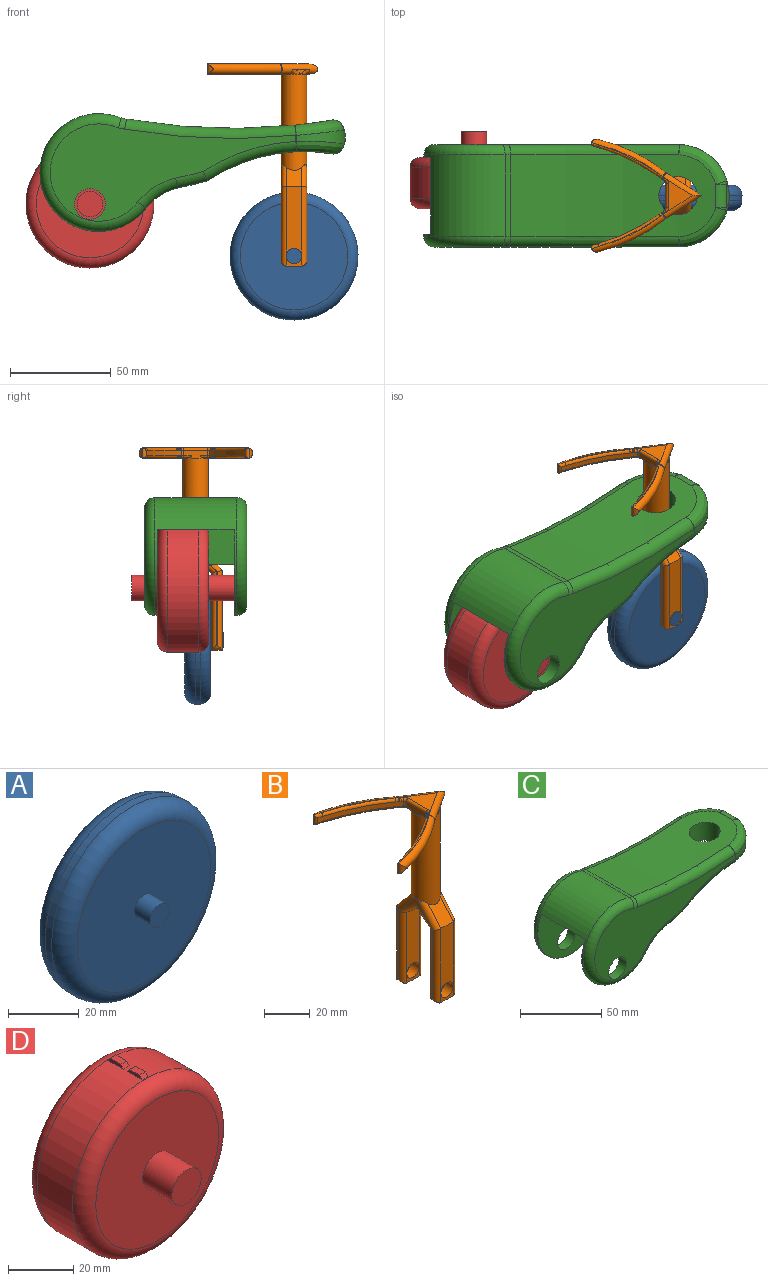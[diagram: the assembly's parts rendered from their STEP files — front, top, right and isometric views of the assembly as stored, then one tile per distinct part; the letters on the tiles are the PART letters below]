
ASSEMBLY  parts=4 mates=3
PART A: 9 faces, bbox 68.7x25.4x68.7 mm
  f0: cylinder r=31.75mm len=63.5mm, axis (0,1,0), area 506.7mm2, adj f7,f8
  f1: plane 53.34x53.34mm, normal (0,-1,0), area 2189mm2, adj f5,f8
  f2: plane 53.34x53.34mm, normal (0,1,0), area 2189mm2, adj f4,f7
  f3: plane 7.62x7.62mm, normal (0,1,0), area 45.6mm2, adj f4
  f4: cylinder r=3.81mm len=7.62mm, axis (0,1,0), area 152mm2, adj f2,f3
  f5: cylinder r=3.81mm len=7.62mm, axis (0,1,0), area 152mm2, adj f1,f6
  f6: plane 7.62x7.62mm, normal (0,-1,0), area 45.6mm2, adj f5
  f7: torus R=26.67mm, axis (0,-1,0), area 1499.3mm2, adj f0,f2
  f8: torus R=26.67mm, axis (0,-1,0), area 1499.3mm2, adj f0,f1
PART B: 110 faces, bbox 59x71.6x101.6 mm
  f0: plane 7.62x4.94mm, normal (0,1,0), area 14.9mm2, adj f19,f88,f99,f109
  f1: plane 7.62x4.94mm, normal (0,-1,0), area 14.9mm2, adj f19,f85,f97,f109
  f2: plane 33.04x7.62mm, normal (0,-1,0), area 229mm2, adj f29,f92,f104,f108
  f3: plane 34.65x7.62mm, normal (0,1,0), area 241.2mm2, adj f30,f93,f103,f108
  f4: plane 36.27x0.13mm, normal (1,0,0), area 4.6mm2, adj f101,f103,f104,f107
  f5: plane 18.75x10.49mm, normal (1,0,0), area 31mm2, adj f98,f100,f102,f105,f106,f107
  f6: plane 36.27x0.13mm, normal (-1,0,0), area 4.6mm2, adj f90,f92,f93,f95
  f7: plane 36.27x0.13mm, normal (-1,0,0), area 4.6mm2, adj f85,f86,f87,f88
  f8: plane 30.79x14.98mm, normal (0,0,1), area 8.5mm2, adj f42,f60
  f9: plane 17.61x13.75mm, normal (0,0,1), area 89.8mm2, adj f43,f47,f70,f74,f76,f77,f79
  f10: plane 30.79x14.98mm, normal (0,0,-1), area 8.5mm2, adj f37,f51
  f11: plane 4.55x4.46mm, normal (0,0,-1), area 4.2mm2, adj f13,f47,f80,f82,f83
  f12: plane 12.1x3.81mm, normal (-1,0,0), area 36.1mm2, adj f13,f14,f63,f71,f77,f81,f83
  f13: cylinder r=6.35mm len=48.93mm, axis (0,0,-1), area 1836.4mm2, adj f11,f12,f14,f17,f23,f27,f30,f39
  f14: plane 4.23x0.36mm, normal (0,0,1), area 1mm2, adj f12,f13
  f15: plane 33.04x7.62mm, normal (0,1,0), area 229mm2, adj f16,f88,f99,f109
  f16: plane 7.88x7.62mm, normal (0,0.63,-0.78), area 77.4mm2, adj f15,f29,f89,f102
  f17: plane 9.44x8.01mm, normal (0,-0.76,0.65), area 84.1mm2, adj f13,f18,f87,f100
  f18: plane 34.65x7.62mm, normal (0,-1,0), area 241.2mm2, adj f17,f85,f97,f109
  f19: plane 7.62x5.21mm, normal (0,0,-1), area 39.7mm2, adj f0,f1,f86,f96
  f20: plane 36.27x0.13mm, normal (1,0,0), area 4.6mm2, adj f96,f97,f99,f100
  f21: plane 18.75x10.49mm, normal (-1,0,0), area 31mm2, adj f84,f87,f89,f91,f94,f95
  f22: plane 30.79x14.98mm, normal (0,0,-1), area 8.5mm2, adj f42,f68
  f23: plane 0.94x0.74mm, normal (0,0,-1), area 0.3mm2, adj f13,f43,f47
  f24: plane 9.55x6.47mm, normal (0.54,0.84,0), area 9.2mm2, adj f45,f47,f48
  f25: plane 30.79x14.98mm, normal (0,0,1), area 8.5mm2, adj f37,f54
  f26: plane 9.55x6.47mm, normal (0.54,-0.84,0), area 9.2mm2, adj f39,f43,f46
  f27: plane 4.55x4.46mm, normal (0,0,-1), area 4.2mm2, adj f13,f43,f62,f63,f67
  f28: plane 7.62x4.94mm, normal (0,-1,0), area 14.9mm2, adj f32,f92,f104,f108
  f29: plane 7.88x7.62mm, normal (0,-0.63,-0.78), area 77.4mm2, adj f2,f16,f91,f105
  f30: plane 9.44x8.01mm, normal (0,0.76,0.65), area 84.1mm2, adj f3,f13,f95,f107
  f31: plane 7.62x4.94mm, normal (0,1,0), area 14.9mm2, adj f32,f93,f103,f108
  f32: plane 7.62x5.21mm, normal (0,0,-1), area 39.7mm2, adj f28,f31,f90,f101
  f33: plane 4.98x0.24mm, normal (-0.87,-0.5,0), area 1.4mm2, adj f37,f38,f50
  f34: cylinder r=101.49mm len=35.64mm, axis (0,0,1), area 101.6mm2, adj f49,f50,f51,f52,f53,f54,f55,f57
  f35: plane 4.98x0.24mm, normal (-0.87,0.5,0), area 1.4mm2, adj f41,f42,f59
  f36: cylinder r=101.49mm len=35.64mm, axis (0,0,1), area 101.6mm2, adj f56,f59,f60,f64,f65,f68,f69,f72
  f37: torus R=82.07mm, axis (0,0,1), area 311.6mm2, adj f10,f25,f33,f38,f40,f49,f50,f52
  f38: cylinder r=2.54mm len=4.84mm, axis (0,0,1), area 7.8mm2, adj f33,f37
  f39: bspline ~5.77x2.86mm, area 6.4mm2, adj f13,f26,f43
  f40: torus R=5.08mm, axis (0,0,1), area 2.9mm2, adj f37,f43,f55,f61
  f41: cylinder r=2.54mm len=4.84mm, axis (0,0,1), area 7.8mm2, adj f35,f42
  f42: torus R=82.07mm, axis (0,0,1), area 311.6mm2, adj f8,f22,f35,f41,f44,f56,f59,f64
  f43: cylinder r=2.54mm len=19.03mm, axis (-0.84,-0.54,0), area 115.1mm2, adj f9,f23,f26,f27,f39,f40,f46,f47
  f44: torus R=5.08mm, axis (0,0,1), area 2.9mm2, adj f42,f47,f69,f75
  f45: bspline ~5.77x2.86mm, area 6.4mm2, adj f13,f24,f47
  f46: bspline ~5.01x4.47mm, area 6.2mm2, adj f13,f26,f43
  f47: cylinder r=2.54mm len=19.03mm, axis (-0.84,0.54,0), area 115.1mm2, adj f9,f11,f23,f24,f43,f44,f45,f48
  f48: bspline ~5.01x4.47mm, area 6.2mm2, adj f13,f24,f47
  f49: bspline ~8.42x3.73mm, area 6.4mm2, adj f34,f37,f50,f51
  f50: cylinder r=1.27mm len=5.06mm, axis (0,0,1), area 9.9mm2, adj f33,f34,f37,f49,f52
  f51: torus R=102.76mm, axis (0,0,1), area 68.1mm2, adj f10,f34,f49,f53
  f52: bspline ~8.42x3.73mm, area 6.4mm2, adj f34,f37,f50,f54
  f53: bspline ~4.52x3.64mm, area 2.4mm2, adj f34,f37,f51,f55
  f54: torus R=102.76mm, axis (0,0,1), area 68.1mm2, adj f25,f34,f52,f57
  f55: bspline ~1.92x1.9mm, area 1.1mm2, adj f34,f40,f53,f58
  f56: bspline ~8.42x3.73mm, area 6.4mm2, adj f36,f42,f59,f60
  f57: bspline ~4.52x3.64mm, area 2.4mm2, adj f34,f37,f54,f61
  f58: bspline ~3.89x3.56mm, area 1.3mm2, adj f34,f43,f55,f62
  f59: cylinder r=1.27mm len=5.06mm, axis (0,0,1), area 9.9mm2, adj f35,f36,f42,f56,f64
  f60: torus R=102.76mm, axis (0,0,1), area 68.1mm2, adj f8,f36,f56,f65
  f61: bspline ~1.98x1.98mm, area 1.1mm2, adj f34,f40,f57,f66
  f62: torus R=102.76mm, axis (0,0,1), area 2.4mm2, adj f27,f34,f58,f67
  f63: cylinder r=1.27mm len=3.93mm, axis (0,1,0), area 5.7mm2, adj f12,f13,f27,f67
  f64: bspline ~8.42x3.73mm, area 6.4mm2, adj f36,f42,f59,f68
  f65: bspline ~4.52x3.64mm, area 2.4mm2, adj f36,f42,f60,f69
  f66: bspline ~3.89x3.56mm, area 1.3mm2, adj f34,f43,f61,f70
  f67: torus R=2.54mm, axis (0,0,1), area 3.2mm2, adj f27,f62,f63,f71
  f68: torus R=102.76mm, axis (0,0,1), area 68.1mm2, adj f22,f36,f64,f72
  f69: bspline ~1.92x1.9mm, area 1.1mm2, adj f36,f44,f65,f73
  f70: torus R=102.76mm, axis (0,0,1), area 2.4mm2, adj f9,f34,f66,f74
  f71: cylinder r=1.27mm len=2.54mm, axis (0,0,1), area 3mm2, adj f12,f34,f67,f74
  f72: bspline ~4.52x3.64mm, area 2.4mm2, adj f36,f42,f68,f75
  f73: bspline ~3.89x3.56mm, area 1.3mm2, adj f36,f47,f69,f76
  f74: torus R=2.54mm, axis (0,0,1), area 3.2mm2, adj f9,f70,f71,f77
  f75: bspline ~1.98x1.98mm, area 1.1mm2, adj f36,f44,f72,f78
  f76: torus R=102.76mm, axis (0,0,1), area 2.4mm2, adj f9,f36,f73,f79
  f77: cylinder r=1.27mm len=12.1mm, axis (0,1,0), area 24.1mm2, adj f9,f12,f74,f79
  f78: bspline ~3.89x3.56mm, area 1.3mm2, adj f36,f47,f75,f80
  f79: torus R=2.54mm, axis (0,0,1), area 3.2mm2, adj f9,f76,f77,f81
  f80: torus R=102.76mm, axis (0,0,1), area 2.4mm2, adj f11,f36,f78,f82
  f81: cylinder r=1.27mm len=2.54mm, axis (0,0,1), area 3mm2, adj f12,f36,f79,f82
  f82: torus R=2.54mm, axis (0,0,1), area 3.2mm2, adj f11,f80,f81,f83
  f83: cylinder r=1.27mm len=3.93mm, axis (0,-1,0), area 5.7mm2, adj f11,f12,f13,f82
  f84: bspline ~3.77x2.18mm, area 1.6mm2, adj f13,f21,f87
  f85: cylinder r=2.54mm len=39.59mm, axis (0,0,-1), area 151mm2, adj f1,f7,f18,f86,f87
  f86: cylinder r=2.54mm len=5.21mm, axis (0,1,0), area 13.4mm2, adj f7,f19,f85,f88
  f87: cylinder r=2.54mm len=12.75mm, axis (0,-0.65,-0.76), area 54.4mm2, adj f7,f13,f17,f21,f84,f85,f88,f89
  f88: cylinder r=2.54mm len=39.14mm, axis (0,0,1), area 149.6mm2, adj f0,f7,f15,f86,f87,f89
  f89: cylinder r=2.54mm len=11.98mm, axis (0,0.78,0.63), area 46.9mm2, adj f16,f21,f87,f88,f91
  f90: cylinder r=2.54mm len=5.21mm, axis (0,-1,0), area 13.4mm2, adj f6,f32,f92,f93
  f91: cylinder r=2.54mm len=11.98mm, axis (0,-0.78,0.63), area 46.9mm2, adj f21,f29,f89,f92,f95
  f92: cylinder r=2.54mm len=39.14mm, axis (0,0,1), area 149.6mm2, adj f2,f6,f28,f90,f91,f95
  f93: cylinder r=2.54mm len=39.59mm, axis (0,0,-1), area 151mm2, adj f3,f6,f31,f90,f95
  f94: bspline ~3.77x2.18mm, area 1.6mm2, adj f13,f21,f95
  f95: cylinder r=2.54mm len=12.75mm, axis (0,0.65,-0.76), area 54.4mm2, adj f6,f13,f21,f30,f91,f92,f93,f94
  f96: cylinder r=2.54mm len=5.21mm, axis (0,-1,0), area 13.4mm2, adj f19,f20,f97,f99
  f97: cylinder r=2.54mm len=39.59mm, axis (0,0,1), area 151mm2, adj f1,f18,f20,f96,f100
  f98: bspline ~3.77x2.18mm, area 1.6mm2, adj f5,f13,f100
  f99: cylinder r=2.54mm len=39.14mm, axis (0,0,-1), area 149.6mm2, adj f0,f15,f20,f96,f100,f102
  f100: cylinder r=2.54mm len=12.75mm, axis (0,0.65,0.76), area 54.4mm2, adj f5,f13,f17,f20,f97,f98,f99,f102
  f101: cylinder r=2.54mm len=5.21mm, axis (0,1,0), area 13.4mm2, adj f4,f32,f103,f104
  f102: cylinder r=2.54mm len=11.98mm, axis (0,-0.78,-0.63), area 46.9mm2, adj f5,f16,f99,f100,f105
  f103: cylinder r=2.54mm len=39.59mm, axis (0,0,1), area 151mm2, adj f3,f4,f31,f101,f107
  f104: cylinder r=2.54mm len=39.14mm, axis (0,0,-1), area 149.6mm2, adj f2,f4,f28,f101,f105,f107
  f105: cylinder r=2.54mm len=11.98mm, axis (0,0.78,-0.63), area 46.9mm2, adj f5,f29,f102,f104,f107
  f106: bspline ~3.77x2.18mm, area 1.6mm2, adj f5,f13,f107
  f107: cylinder r=2.54mm len=12.75mm, axis (0,-0.65,0.76), area 54.4mm2, adj f4,f5,f13,f30,f103,f104,f105,f106
  f108: cylinder r=3.81mm len=7.62mm, axis (0,1,0), area 124.6mm2, adj f2,f3,f28,f31
  f109: cylinder r=3.81mm len=7.62mm, axis (0,1,0), area 124.6mm2, adj f0,f1,f15,f18
PART C: 53 faces, bbox 153.9x50.9x63.3 mm
  f0: plane 38.1x28.36mm, normal (0,0,-1), area 1080.7mm2, adj f16,f17,f18,f50
  f1: cylinder r=28.25mm len=15.73mm, axis (0,1,0), area 24mm2, adj f2,f6,f17,f27
  f2: cylinder r=225.55mm len=14.86mm, axis (0,1,0), area 19.4mm2, adj f1,f3,f17,f29
  f3: cylinder r=85.3mm len=61.7mm, axis (0,1,0), area 2195mm2, adj f2,f8,f14,f18,f24,f31,f42,f44
  f4: cylinder r=13.12mm len=10.14mm, axis (0,1,0), area 26.3mm2, adj f44,f45
  f5: cylinder r=299.81mm len=101.73mm, axis (0,1,0), area 3719.3mm2, adj f10,f14,f23,f30,f34,f37,f39
  f6: cylinder r=29.25mm len=58.5mm, axis (0,1,0), area 1978.8mm2, adj f1,f7,f10,f15,f16,f17,f19,f26
  f7: cylinder r=28.25mm len=15.73mm, axis (0,1,0), area 24mm2, adj f6,f8,f16,f20
  f8: cylinder r=225.55mm len=14.86mm, axis (0,1,0), area 19.4mm2, adj f3,f7,f16,f22
  f9: cylinder r=13.12mm len=11.48mm, axis (0,1,0), area 34.1mm2, adj f36,f37
  f10: cylinder r=38.9mm len=40.64mm, axis (0,1,0), area 115mm2, adj f5,f6,f21,f28
  f11: plane 121.94x48.34mm, normal (0,-1,0), area 2650.8mm2, adj f19,f20,f21,f22,f23,f24,f25,f52
  f12: plane 121.94x48.34mm, normal (0,1,0), area 2650.8mm2, adj f26,f27,f28,f29,f30,f31,f32,f51
  f13: cylinder r=25.42mm len=50.79mm, axis (0,0,-1), area 355.2mm2, adj f25,f32,f34,f36,f39,f42,f45,f47
  f14: cylinder r=9.53mm len=19.05mm, axis (0,0,-1), area 810.4mm2, adj f3,f5
  f15: plane 38.1x3.17mm, normal (0,0,-1), area 120.8mm2, adj f6,f16,f17,f49
  f16: plane 83.25x55.8mm, normal (0,1,0), area 2890.1mm2, adj f0,f6,f7,f8,f15,f18,f49,f50
  f17: plane 83.25x55.8mm, normal (0,-1,0), area 2890.1mm2, adj f0,f1,f2,f6,f15,f18,f49,f50
  f18: plane 38.1x17.53mm, normal (-1,0,0), area 667.9mm2, adj f0,f3,f16,f17
  f19: torus R=24.17mm, axis (0,-1,0), area 976.3mm2, adj f6,f11,f20,f21
  f20: torus R=33.33mm, axis (0,-1,0), area 161.3mm2, adj f7,f11,f19,f22
  f21: torus R=33.82mm, axis (0,-1,0), area 23.8mm2, adj f10,f11,f19,f23
  f22: torus R=220.47mm, axis (0,-1,0), area 118.9mm2, adj f8,f11,f20,f24
  f23: torus R=304.89mm, axis (0,-1,0), area 673.3mm2, adj f5,f11,f21,f33
  f24: torus R=90.38mm, axis (0,-1,0), area 379.9mm2, adj f3,f11,f22,f41
  f25: cylinder r=5.08mm len=3.05mm, axis (0,0,-1), area 0.7mm2, adj f11,f13,f33,f41
  f26: torus R=24.17mm, axis (0,-1,0), area 976.3mm2, adj f6,f12,f27,f28
  f27: torus R=33.33mm, axis (0,-1,0), area 161.3mm2, adj f1,f12,f26,f29
  f28: torus R=33.82mm, axis (0,-1,0), area 23.8mm2, adj f10,f12,f26,f30
  f29: torus R=220.47mm, axis (0,-1,0), area 118.9mm2, adj f2,f12,f27,f31
  f30: torus R=304.89mm, axis (0,-1,0), area 673.3mm2, adj f5,f12,f28,f40
  f31: torus R=90.38mm, axis (0,-1,0), area 379.9mm2, adj f3,f12,f29,f48
  f32: cylinder r=5.08mm len=3.05mm, axis (0,0,-1), area 0.7mm2, adj f12,f13,f40,f48
  f33: sphere r=5.08mm, area 1.2mm2, adj f23,f25,f34
  f34: bspline ~27.69x20.92mm, area 246.4mm2, adj f5,f13,f33,f35
  f35: sphere r=5.08mm, area 7mm2, adj f34,f36,f37
  f36: bspline ~18.47x7.43mm, area 22.2mm2, adj f9,f13,f35,f38
  f37: cylinder r=5.08mm len=11.48mm, axis (0,-1,0), area 74.5mm2, adj f5,f9,f35,f38
  f38: sphere r=5.08mm, area 7mm2, adj f36,f37,f39
  f39: bspline ~27.69x20.92mm, area 246.4mm2, adj f5,f13,f38,f40
  f40: sphere r=5.08mm, area 1.2mm2, adj f30,f32,f39
  f41: sphere r=5.08mm, area 1.2mm2, adj f24,f25,f42
  f42: bspline ~26.23x22.17mm, area 246mm2, adj f3,f13,f41,f43
  f43: sphere r=5.08mm, area 6.3mm2, adj f42,f44,f45
  f44: cylinder r=5.08mm len=10.14mm, axis (0,-1,0), area 68.6mm2, adj f3,f4,f43,f46
  f45: bspline ~15.84x6.2mm, area 17.3mm2, adj f4,f13,f43,f46
  f46: sphere r=5.08mm, area 6.3mm2, adj f44,f45,f47
  f47: bspline ~26.23x22.17mm, area 246mm2, adj f3,f13,f46,f48
  f48: sphere r=5.08mm, area 1.2mm2, adj f31,f32,f47
  f49: cylinder r=26.47mm len=44.32mm, axis (0,-1,0), area 2004.2mm2, adj f15,f16,f17,f50
  f50: cylinder r=5.08mm len=38.1mm, axis (0,-1,0), area 183.1mm2, adj f0,f16,f17,f49
  f51: cylinder r=7.62mm len=15.24mm, axis (0,-1,0), area 304mm2, adj f12,f17
  f52: cylinder r=7.62mm len=15.24mm, axis (0,-1,0), area 304mm2, adj f11,f16
PART D: 19 faces, bbox 68.7x50.8x68.7 mm
  f0: cylinder r=31.75mm len=63.5mm, axis (0,1,0), area 3006.8mm2, adj f7,f8,f10,f11,f12,f13,f14,f15
  f1: plane 53.34x53.34mm, normal (0,-1,0), area 2107.9mm2, adj f5,f8
  f2: plane 53.34x53.34mm, normal (0,1,0), area 2107.9mm2, adj f4,f7
  f3: plane 12.7x12.7mm, normal (0,1,0), area 126.7mm2, adj f4
  f4: cylinder r=6.35mm len=12.7mm, axis (0,1,0), area 506.7mm2, adj f2,f3
  f5: cylinder r=6.35mm len=12.7mm, axis (0,1,0), area 506.7mm2, adj f1,f6
  f6: plane 12.7x12.7mm, normal (0,-1,0), area 126.7mm2, adj f5
  f7: torus R=26.67mm, axis (0,-1,0), area 1499.3mm2, adj f0,f2
  f8: torus R=26.67mm, axis (0,-1,0), area 1499.3mm2, adj f0,f1
  f9: plane 4.29x2.54mm, normal (0,0,1), area 10.9mm2, adj f10,f11,f12,f13
  f10: plane 6.53x1.27mm, normal (1,0,0), area 6.8mm2, adj f0,f9,f12,f13
  f11: plane 6.53x1.27mm, normal (-1,0,0), area 6.8mm2, adj f0,f9,f12,f13
  f12: plane 2.54x1.27mm, normal (0,0.74,0.67), area 4.3mm2, adj f0,f9,f10,f11
  f13: plane 2.54x1.27mm, normal (0,-0.76,0.66), area 4.2mm2, adj f0,f9,f10,f11
  f14: plane 6.68x1.27mm, normal (1,0,0), area 7.2mm2, adj f0,f16,f17,f18
  f15: plane 6.68x1.27mm, normal (-1,0,0), area 7.2mm2, adj f0,f16,f17,f18
  f16: plane 2.54x1.27mm, normal (0,0.79,0.61), area 4mm2, adj f0,f14,f15,f17
  f17: plane 4.65x2.54mm, normal (0,0,1), area 11.8mm2, adj f14,f15,f16,f18
  f18: plane 2.54x1.27mm, normal (0,-0.76,0.64), area 4.1mm2, adj f0,f14,f15,f17
PLACE A t=(57.26,16.58,-68.98)mm
PLACE B t=(57.26,17.54,-29.53)mm
PLACE C t=(14.43,17.54,-39.5)mm
PLACE D rot(axis=(0,0,1),0deg) t=(-43.99,23.89,-43.17)mm
MATE revolute A.f4 <-> B.f108  axis (0,1,0) through (57.26,7.05,-68.98)mm
MATE cylindrical B.f13 <-> C.f13  axis (0,0,-1) through (57.26,17.54,22.84)mm
MATE revolute D.f4 <-> C.f51  axis (0,1,0) through (-43.99,42.94,-43.17)mm
